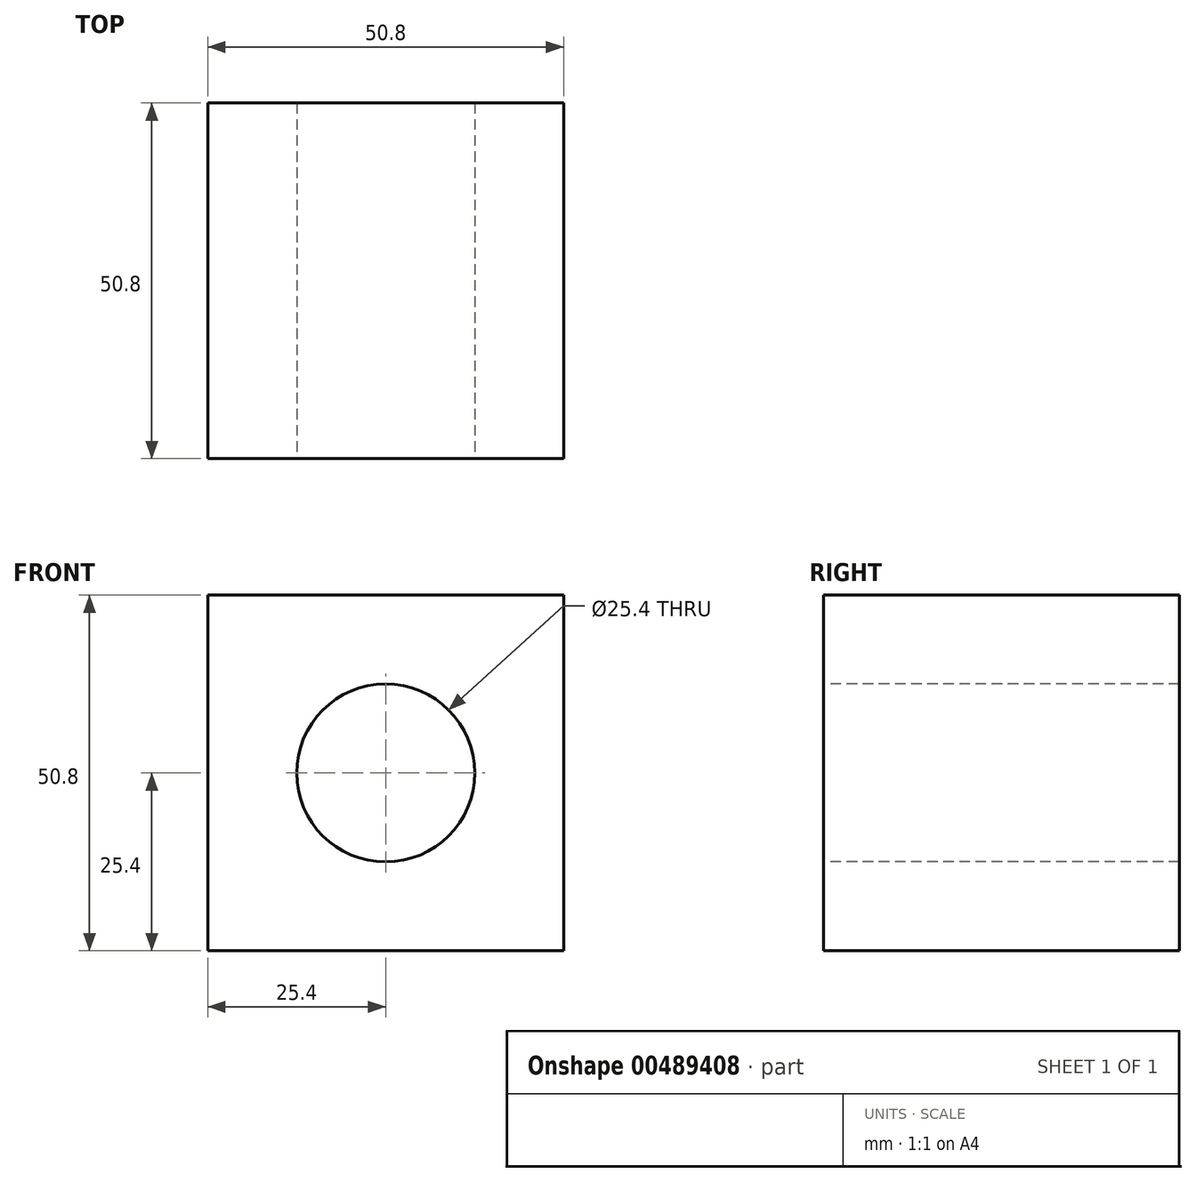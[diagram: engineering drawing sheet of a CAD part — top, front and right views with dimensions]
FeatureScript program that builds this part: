
annotation { "Feature Type Name" : "Feature", "Feature Type Description" : "" }
export const myFeature = defineFeature(function(context is Context, id is Id, definition is map)
    precondition{}
    {
        {
            var Q0;
            Q0=qCreatedBy(makeId("Front.planeOp"),FACE);
            var sketch = newSketch(context, id + "F0", { "sketchPlane" : qUnion([Q0])});
            skLineSegment(sketch, "E0", {"start": v(0, 0) * mm, "end": v(0, 50.8) * mm});
            skLineSegment(sketch, "E1", {"start": v(0, 50.8) * mm, "end": v(50.8, 50.8) * mm});
            skLineSegment(sketch, "E2", {"start": v(50.8, 50.8) * mm, "end": v(50.8, 0) * mm});
            skLineSegment(sketch, "E3", {"start": v(50.8, 0) * mm, "end": v(0, 0) * mm});
            skSolve(sketch);
        }
        {
            var Q0;
            Q0=makeQuery(id+"F0.imprint","IMPRINT",FACE,{"disambiguationData":[TD([[makeQuery(id+"F0.imprint","IMPRINT",EDGE,{"derivedFrom":sQuery(id+"F0.wireOp",EDGE,"E0")}),-1.0]])]});
            extrude(context, id + "F1", {"entities" : qUnion([Q0]), "depth" : 50.8 * mm});
        }
        {
            var Q0;
            Q0=makeQuery(id+"F1.opExtrude","CAP_FACE",FACE,{"disambiguationData":[OSD([sQuery(id+"F0.wireOp",EDGE,"E0"),sQuery(id+"F0.wireOp",EDGE,"E1"),sQuery(id+"F0.wireOp",EDGE,"E2"),sQuery(id+"F0.wireOp",EDGE,"E3")])],"isStart":false});
            var sketch = newSketch(context, id + "F2", { "sketchPlane" : qUnion([Q0])});
            skCircle(sketch, "E4", {"center": v(25.4, 25.4) * mm, "radius": 12.7 * mm});
            skPoint(sketch, "E4.centerSnap0", {"position": v(50.8, 25.4) * mm});
            skPoint(sketch, "E4.centerSnap1", {"position": v(25.4, 50.8) * mm});
            skSolve(sketch);
        }
        {
            var Q0;
            Q0=makeQuery(id+"F2.imprint","IMPRINT",FACE,{"disambiguationData":[TD([[makeQuery(id+"F2.imprint","IMPRINT",EDGE,{"derivedFrom":sQuery(id+"F2.wireOp",EDGE,"E4")}),1.0]])]});
            extrude(context, id + "F3", {"entities" : qUnion([Q0]), "operationType" : NewBodyOperationType.REMOVE, "oppositeDirection" : true, "depth" : 50.8 * mm});
        }
    });
